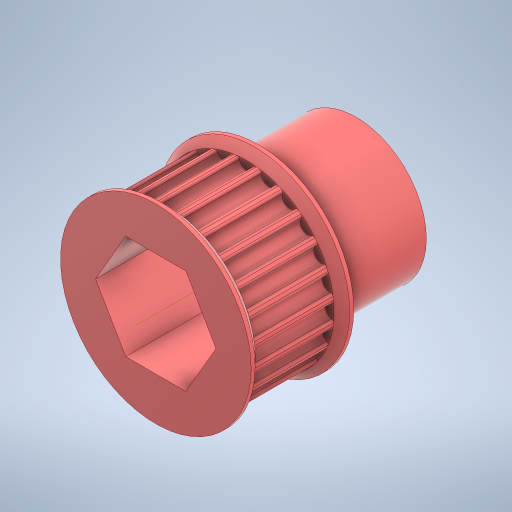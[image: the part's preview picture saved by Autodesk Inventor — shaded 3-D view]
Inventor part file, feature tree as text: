
AUTODESK INVENTOR PART (.ipt)
format: ipt  version: 2023.3 (Build 273359000, 359)  size: 498,688 bytes
history: native  units: in
note: dims shown in document units (in); Inventor stores cm internally (conversion verified against a paired STEP export)
features: extrude x7, sketch x7, mirror x2, chamfer x2, other x1, fillet x1, pattern_circular x1
ambient origin geometry x8: Origin, YZ Plane, XZ Plane, XY Plane, X Axis, Y Axis, Z Axis, Center Point
bodies: Solid1 (feature_tree)
feature tree (21):
  other  "Hex Bore"
  extrude  "HTD Base"  Depth=0.3937in TaperAngle=0.0deg
  extrude  "HTD Flange"  Depth=0.0591in
  mirror  "HTD Flanges"
  chamfer  "HTD Flange Chamfer"  Distance=0.0787in Angle=45.0deg
  extrude  "GT2 Base"  TaperAngle=0.0deg  [1 undecoded]
  extrude  "GT2 Base Tooth"  TaperAngle=0.0deg  [1 undecoded]
  fillet  "GT2 Base Tooth pt. 2"  Radius=0.8723in
  pattern_circular  "GT2 Teeth"  [2 undecoded]
  extrude  "GT2 Flange"  Depth=0.4875in
  mirror  "GT2 Flanges"
  chamfer  "GT2 Flange Chamfer"  Distance=0.0075in
  extrude  "Circle Bore"  TaperAngle=0.0deg  [1 undecoded]
  extrude  "Extrusion9"  Depth=0.0118in
  sketch  "Sketch1"  dims[d0=1.4588in d1=0.3937in d2=0.0in]
  sketch  "Sketch4"  dims[d12=0.0394in d13=0.0591in]
  sketch  "Sketch5"  dims[d14=0.0in]
  sketch  "Sketch6"  dims[d15=0.0394in d16=0.0787in d17=45.0deg]
  sketch  "Sketch7"  dims[d18=0.52in d19=0.0in d20=0.0in]
  sketch  "Sketch8"  dims[d21=0.52in d22=0.0in d23=0.0in d24=0.8723in]
  sketch  "Sketch9"  dims[d25=0.3937in d26=0.0in d27=0.0727in d28=0.0075in d29=0.0in d30=0.0in d31=0.0118in d32=9.4488in d33=360.0deg d35=0.0394in d36=0.0591in d37=0.0in d38=0.0394in d39=0.0787in d40=45.0deg d41=0.05in d42=0.4875in d43=0.0in]
note: 5 required parameter values undecoded (feature->parameter linkage not recoverable at this tier; creation-order binding heuristic only, values carry confidence <= 0.55)
